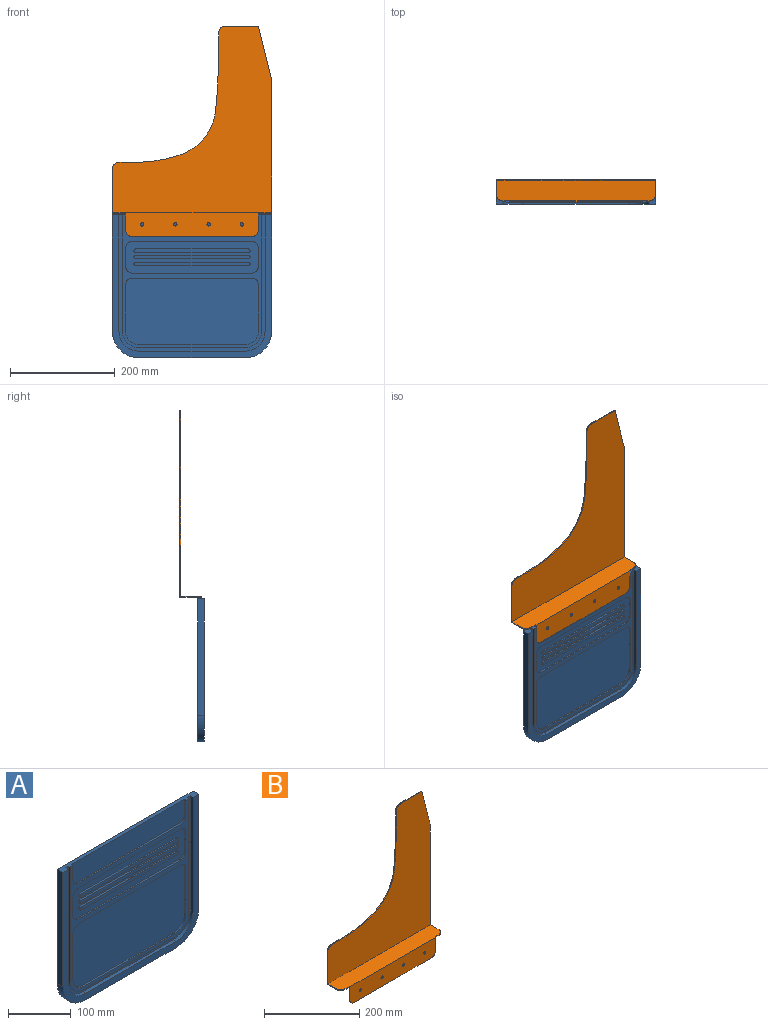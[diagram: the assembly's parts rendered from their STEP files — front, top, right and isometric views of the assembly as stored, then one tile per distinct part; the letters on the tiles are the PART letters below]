
ASSEMBLY  parts=2 mates=1
PART A: 59 faces, bbox 304.8x12.7x273.1 mm
  f0: plane 279.4x260.35mm, normal (0,-1,0), area 4809.6mm2, adj f3,f7,f8,f15,f16,f17,f18,f29
  f1: plane 254x41.28mm, normal (0,-1,0), area 10414.6mm2, adj f5,f6,f26,f27,f28,f58
  f2: plane 222.25x12.7mm, normal (1,0,0), area 2822.6mm2, adj f4,f12,f14,f58
  f3: plane 222.25x6.35mm, normal (-1,0,0), area 1411.3mm2, adj f0,f4,f15,f58
  f4: plane 304.8x273.05mm, normal (0,-1,0), area 9999.3mm2, adj f2,f3,f10,f11,f13,f14,f15,f16
  f5: plane 28.58x3.18mm, normal (-1,0,0), area 90.7mm2, adj f1,f9,f26,f58
  f6: plane 28.58x3.18mm, normal (1,0,0), area 90.7mm2, adj f1,f9,f28,f58
  f7: plane 222.25x3.18mm, normal (-1,0,0), area 705.6mm2, adj f0,f9,f29,f58
  f8: plane 222.25x3.18mm, normal (1,0,0), area 705.6mm2, adj f0,f9,f31,f58
  f9: plane 266.7x254mm, normal (0,-1,0), area 9798.5mm2, adj f5,f6,f7,f8,f19,f20,f21,f22
  f10: plane 222.25x12.7mm, normal (-1,0,0), area 2822.6mm2, adj f4,f12,f13,f58
  f11: plane 203.2x12.7mm, normal (0,0,-1), area 2580.6mm2, adj f4,f12,f13,f14
  f12: plane 304.8x273.05mm, normal (0,1,0), area 82118mm2, adj f2,f10,f11,f13,f14,f58
  f13: cylinder r=50.8mm len=50.8mm, axis (0,-1,0), area 1013.4mm2, adj f4,f10,f11,f12
  f14: cylinder r=50.8mm len=50.8mm, axis (0,1,0), area 1013.4mm2, adj f2,f4,f11,f12
  f15: cylinder r=38.1mm len=38.1mm, axis (0,1,0), area 380mm2, adj f0,f3,f4,f16
  f16: plane 203.2x6.35mm, normal (0,0,1), area 1290.3mm2, adj f0,f4,f15,f17
  f17: cylinder r=38.1mm len=38.1mm, axis (0,1,0), area 380mm2, adj f0,f4,f16,f18
  f18: plane 222.25x6.35mm, normal (1,0,0), area 1411.3mm2, adj f0,f4,f17,f58
  f19: cylinder r=12.7mm len=12.7mm, axis (0,1,0), area 63.3mm2, adj f9,f20,f40,f42
  f20: plane 228.6x3.18mm, normal (0,0,-1), area 725.8mm2, adj f9,f19,f21,f42
  f21: cylinder r=12.7mm len=12.7mm, axis (0,1,0), area 63.3mm2, adj f9,f20,f22,f42
  f22: plane 88.9x3.18mm, normal (-1,0,0), area 282.3mm2, adj f9,f21,f23,f42
  f23: cylinder r=25.4mm len=25.4mm, axis (0,1,0), area 126.7mm2, adj f9,f22,f24,f42
  f24: plane 203.2x3.18mm, normal (0,0,1), area 645.2mm2, adj f9,f23,f25,f42
  f25: cylinder r=25.4mm len=25.4mm, axis (0,1,0), area 126.7mm2, adj f9,f24,f40,f42
  f26: cylinder r=12.7mm len=12.7mm, axis (0,1,0), area 63.3mm2, adj f1,f5,f9,f27
  f27: plane 228.6x3.18mm, normal (0,0,1), area 725.8mm2, adj f1,f9,f26,f28
  f28: cylinder r=12.7mm len=12.7mm, axis (0,1,0), area 63.3mm2, adj f1,f6,f9,f27
  f29: cylinder r=31.75mm len=31.75mm, axis (0,1,0), area 158.3mm2, adj f0,f7,f9,f30
  f30: plane 203.2x3.18mm, normal (0,0,-1), area 645.2mm2, adj f0,f9,f29,f31
  f31: cylinder r=31.75mm len=31.75mm, axis (0,1,0), area 158.3mm2, adj f0,f8,f9,f30
  f32: cylinder r=12.7mm len=12.7mm, axis (0,1,0), area 63.3mm2, adj f9,f33,f39,f41
  f33: plane 228.6x3.18mm, normal (0,0,-1), area 725.8mm2, adj f9,f32,f34,f41
  f34: cylinder r=12.7mm len=12.7mm, axis (0,1,0), area 63.3mm2, adj f9,f33,f35,f41
  f35: plane 34.93x3.18mm, normal (-1,0,0), area 110.9mm2, adj f9,f34,f36,f41
  f36: cylinder r=12.7mm len=12.7mm, axis (0,1,0), area 63.3mm2, adj f9,f35,f37,f41
  f37: plane 228.6x3.18mm, normal (0,0,1), area 725.8mm2, adj f9,f36,f38,f41
  f38: cylinder r=12.7mm len=12.7mm, axis (0,1,0), area 63.3mm2, adj f9,f37,f39,f41
  f39: plane 34.93x3.18mm, normal (1,0,0), area 110.9mm2, adj f9,f32,f38,f41
  f40: plane 88.9x3.18mm, normal (1,0,0), area 282.3mm2, adj f9,f19,f25,f42
  f41: plane 254x60.33mm, normal (0,-1,0), area 10976.2mm2, adj f32,f33,f34,f35,f36,f37,f38,f39
  f42: plane 254x127mm, normal (0,-1,0), area 31911.9mm2, adj f19,f20,f21,f22,f23,f24,f25,f40
  f43: plane 215.9x3.18mm, normal (0,0,1), area 685.5mm2, adj f41,f44,f46,f47
  f44: cylinder r=3.17mm len=6.35mm, axis (0,1,0), area 31.7mm2, adj f41,f43,f45,f47
  f45: plane 215.9x3.18mm, normal (0,0,-1), area 685.5mm2, adj f41,f44,f46,f47
  f46: cylinder r=3.17mm len=6.35mm, axis (0,1,0), area 31.7mm2, adj f41,f43,f45,f47
  f47: plane 222.25x6.35mm, normal (0,-1,0), area 1402.6mm2, adj f43,f44,f45,f46
  f48: plane 215.9x3.18mm, normal (0,0,1), area 685.5mm2, adj f41,f49,f51,f52
  f49: cylinder r=3.17mm len=6.35mm, axis (0,1,0), area 31.7mm2, adj f41,f48,f50,f52
  f50: plane 215.9x3.18mm, normal (0,0,-1), area 685.5mm2, adj f41,f49,f51,f52
  f51: cylinder r=3.17mm len=6.35mm, axis (0,1,0), area 31.7mm2, adj f41,f48,f50,f52
  f52: plane 222.25x6.35mm, normal (0,-1,0), area 1402.6mm2, adj f48,f49,f50,f51
  f53: plane 215.9x3.18mm, normal (0,0,1), area 685.5mm2, adj f41,f54,f56,f57
  f54: cylinder r=3.17mm len=6.35mm, axis (0,1,0), area 31.7mm2, adj f41,f53,f55,f57
  f55: plane 215.9x3.18mm, normal (0,0,-1), area 685.5mm2, adj f41,f54,f56,f57
  f56: cylinder r=3.17mm len=6.35mm, axis (0,1,0), area 31.7mm2, adj f41,f53,f55,f57
  f57: plane 222.25x6.35mm, normal (0,-1,0), area 1402.6mm2, adj f53,f54,f55,f56
  f58: plane 304.8x12.7mm, normal (0,0,1), area 2137.1mm2, adj f0,f1,f2,f3,f4,f5,f6,f7
PART B: 30 faces, bbox 304.8x42.2x402.1 mm
  f0: plane 12.7x2.03mm, normal (0,-1,0), area 25.8mm2, adj f14,f15,f18,f23
  f1: cylinder r=101.6mm len=85.79mm, axis (0,1,0), area 235.1mm2, adj f2,f9,f10,f11
  f2: cylinder r=262.16mm len=85.07mm, axis (0,1,0), area 176mm2, adj f1,f3,f10,f11
  f3: plane 31.75x2.03mm, normal (0,0,1), area 64.5mm2, adj f2,f10,f11,f12
  f4: plane 84.58x27.43mm, normal (-1,0,0), area 223.5mm2, adj f10,f11,f12,f14,f15,f23
  f5: plane 256.03x27.43mm, normal (1,0,0), area 571.9mm2, adj f6,f10,f11,f14,f15,f22
  f6: plane 101.6x25.4mm, normal (0.97,0,0.24), area 212.8mm2, adj f5,f7,f10,f11
  f7: plane 63.5x2.03mm, normal (0,0,1), area 129mm2, adj f6,f10,f11,f13
  f8: plane 38.1x2.03mm, normal (-1,0,0), area 77.4mm2, adj f9,f10,f11,f13
  f9: cylinder r=1079.5mm len=109.58mm, axis (0,1,0), area 223mm2, adj f1,f8,f10,f11
  f10: plane 355.6x304.8mm, normal (0,-1,0), area 57980.3mm2, adj f1,f2,f3,f4,f5,f6,f7,f8
  f11: plane 357.63x304.8mm, normal (0,1,0), area 58599.7mm2, adj f1,f2,f3,f4,f5,f6,f7,f8
  f12: cylinder r=12.7mm len=12.7mm, axis (0,-1,0), area 40.5mm2, adj f3,f4,f10,f11
  f13: cylinder r=12.7mm len=12.7mm, axis (0,1,0), area 40.5mm2, adj f7,f8,f10,f11
  f14: plane 304.8x40.13mm, normal (0,0,1), area 12059.8mm2, adj f0,f4,f5,f10,f16,f18,f20,f21
  f15: plane 304.8x40.13mm, normal (0,0,-1), area 12163mm2, adj f0,f4,f5,f11,f16,f17,f22,f23
  f16: plane 12.7x2.03mm, normal (0,-1,0), area 25.8mm2, adj f14,f15,f20,f22
  f17: plane 254x44.45mm, normal (0,1,0), area 11094.4mm2, adj f15,f18,f19,f20,f24,f25,f26,f27
  f18: plane 33.78x2.03mm, normal (-1,0,0), area 68.6mm2, adj f0,f14,f17,f21,f24
  f19: plane 228.6x2.03mm, normal (0,0,-1), area 464.5mm2, adj f17,f21,f24,f25
  f20: plane 33.78x2.03mm, normal (1,0,0), area 68.6mm2, adj f14,f16,f17,f21,f25
  f21: plane 254x46.48mm, normal (0,-1,0), area 11610.5mm2, adj f14,f18,f19,f20,f24,f25,f26,f27
  f22: cylinder r=12.7mm len=12.7mm, axis (0,0,-1), area 40.5mm2, adj f5,f14,f15,f16
  f23: cylinder r=12.7mm len=12.7mm, axis (0,0,-1), area 40.5mm2, adj f0,f4,f14,f15
  f24: cylinder r=12.7mm len=12.7mm, axis (0,1,0), area 40.5mm2, adj f17,f18,f19,f21
  f25: cylinder r=12.7mm len=12.7mm, axis (0,-1,0), area 40.5mm2, adj f17,f19,f20,f21
  f26: cylinder r=3.17mm len=6.35mm, axis (0,-1,0), area 40.5mm2, adj f17,f21
  f27: cylinder r=3.17mm len=6.35mm, axis (0,-1,0), area 40.5mm2, adj f17,f21
  f28: cylinder r=3.17mm len=6.35mm, axis (0,-1,0), area 40.5mm2, adj f17,f21
  f29: cylinder r=3.17mm len=6.35mm, axis (0,-1,0), area 40.5mm2, adj f17,f21
PLACE A t=(-152.4,12.7,0)mm fixed
PLACE B t=(-152.4,46.48,278.26)mm
MATE fastened B.f17 <-> A.f1  axis (0,1,0) through (0,6.35,231.78)mm
